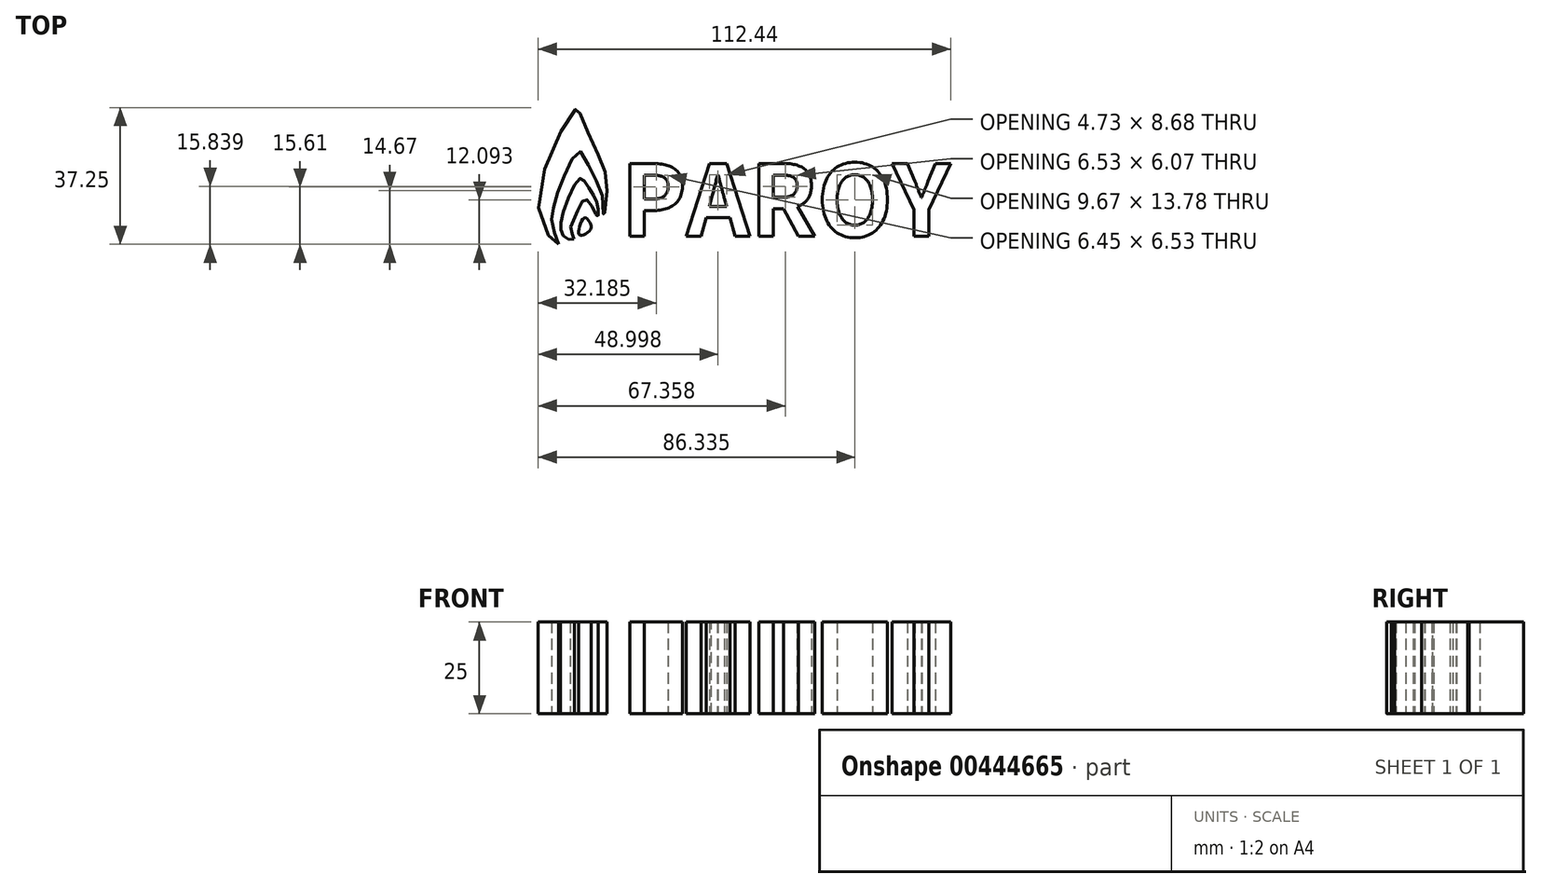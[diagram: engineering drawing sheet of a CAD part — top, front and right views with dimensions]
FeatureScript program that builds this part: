
annotation { "Feature Type Name" : "Feature", "Feature Type Description" : "" }
export const myFeature = defineFeature(function(context is Context, id is Id, definition is map)
    precondition{}
    {
        {
            var Q0;
            Q0=qCreatedBy(makeId("Top.planeOp"),FACE);
            var sketch = newSketch(context, id + "F0", { "sketchPlane" : qUnion([Q0])});
            skFitSpline(sketch, "E0", {"points": [v(11.09, 18.28) * mm, v(5.6, 28.42) * mm, v(16.23, 55.43) * mm, v(16.82, 54.37) * mm, v(21.96, 42.44) * mm, v(24.32, 33.84) * mm, v(23.38, 25.59) * mm, v(23.02, 31.36) * mm, v(20.14, 37.78) * mm, v(16.83, 43.57) * mm, v(13.73, 39.2) * mm, v(10.53, 31.36) * mm, v(9.34, 26.1) * mm, v(9.55, 22.62) * mm, v(11.09, 18.28) * mm]});
            skSolve(sketch);
        }
        {
            var Q0;
            Q0=makeQuery(id+"F0.imprint","IMPRINT",FACE,{"disambiguationData":[TD([[makeQuery(id+"F0.imprint","IMPRINT",EDGE,{"derivedFrom":sQuery(id+"F0.wireOp",EDGE,"E0")}),-1.0]])]});
            extrude(context, id + "F1", {"entities" : qUnion([Q0]), "depth" : 25 * mm});
        }
        {
            var Q0;
            Q0=qCreatedBy(makeId("Top.planeOp"),FACE);
            var sketch = newSketch(context, id + "F2", { "sketchPlane" : qUnion([Q0])});
            skFitSpline(sketch, "E1", {"points": [v(15.34, 19.65) * mm, v(13.4, 19.76) * mm, v(11.81, 21.9) * mm, v(12.22, 26.48) * mm, v(16.88, 36.14) * mm, v(18.32, 35.25) * mm, v(20.86, 31.2) * mm, v(21.9, 27.87) * mm, v(21.78, 25.84) * mm, v(20.58, 27.8) * mm, v(18.21, 30.52) * mm, v(15.47, 25.22) * mm, v(14.39, 22.32) * mm, v(15.34, 19.65) * mm]});
            skSolve(sketch);
        }
        {
            var Q0;
            Q0=qCreatedBy(makeId("Top.planeOp"),FACE);
            var sketch = newSketch(context, id + "F3", { "sketchPlane" : qUnion([Q0])});
            skFitSpline(sketch, "E2", {"points": [v(16.83, 23.07) * mm, v(18.3, 25.48) * mm, v(19.68, 24.09) * mm, v(19.93, 22.42) * mm, v(17.79, 20.75) * mm, v(16.7, 20.92) * mm, v(16.83, 23.07) * mm]});
            skSolve(sketch);
        }
        {
            var Q0;
            Q0=makeQuery(id+"F3.imprint","IMPRINT",FACE,{"disambiguationData":[TD([[makeQuery(id+"F3.imprint","IMPRINT",EDGE,{"derivedFrom":sQuery(id+"F3.wireOp",EDGE,"E2")}),-1.0]])]});
            extrude(context, id + "F4", {"entities" : qUnion([Q0]), "depth" : 25 * mm});
        }
        {
            var Q0;
            Q0=makeQuery(id+"F2.imprint","IMPRINT",FACE,{"disambiguationData":[TD([[makeQuery(id+"F2.imprint","IMPRINT",EDGE,{"derivedFrom":sQuery(id+"F2.wireOp",EDGE,"E1")}),-1.0]])]});
            extrude(context, id + "F5", {"entities" : qUnion([Q0]), "depth" : 25 * mm});
        }
        {
            var Q0;
            Q0=qCreatedBy(makeId("Top.planeOp"),FACE);
            var sketch = newSketch(context, id + "F6", { "sketchPlane" : qUnion([Q0])});
            skText(sketch, "E3", { "text": "PAROY", "fontName": "NotoSansCJKtc-Bold.otf"});
            const initialGuessF6  = {"E3": [0.0281, 0.02036, 1, 0, 0.01934]};
            skSetInitialGuess(sketch, initialGuessF6);
            skSolve(sketch);
        }
        {
            var Q0;
            Q0=makeQuery(id+"F6.imprint","IMPRINT",FACE,{"disambiguationData":[TD([[makeQuery(id+"F6.imprint","IMPRINT",EDGE,{"derivedFrom":sQuery(id+"F6.wireOp",EDGE,"E3.sketch_text.stroke-49")}),1.0]])]});
            var Q1;
            Q1=makeQuery(id+"F6.imprint","IMPRINT",FACE,{"disambiguationData":[TD([[makeQuery(id+"F6.imprint","IMPRINT",EDGE,{"derivedFrom":sQuery(id+"F6.wireOp",EDGE,"E3.sketch_text.stroke-41")}),1.0]])]});
            var Q2;
            Q2=makeQuery(id+"F6.imprint","IMPRINT",FACE,{"disambiguationData":[TD([[makeQuery(id+"F6.imprint","IMPRINT",EDGE,{"derivedFrom":sQuery(id+"F6.wireOp",EDGE,"E3.sketch_text.stroke-26")}),1.0]])]});
            var Q3;
            Q3=makeQuery(id+"F6.imprint","IMPRINT",FACE,{"disambiguationData":[TD([[makeQuery(id+"F6.imprint","IMPRINT",EDGE,{"derivedFrom":sQuery(id+"F6.wireOp",EDGE,"E3.sketch_text.stroke-12")}),1.0]])]});
            var Q4;
            Q4=makeQuery(id+"F6.imprint","IMPRINT",FACE,{"disambiguationData":[TD([[makeQuery(id+"F6.imprint","IMPRINT",EDGE,{"derivedFrom":sQuery(id+"F6.wireOp",EDGE,"E3.sketch_text.stroke-0")}),1.0]])]});
            extrude(context, id + "F7", {"entities" : qUnion([Q0, Q1, Q2, Q3, Q4]), "depth" : 25 * mm});
        }
    });
